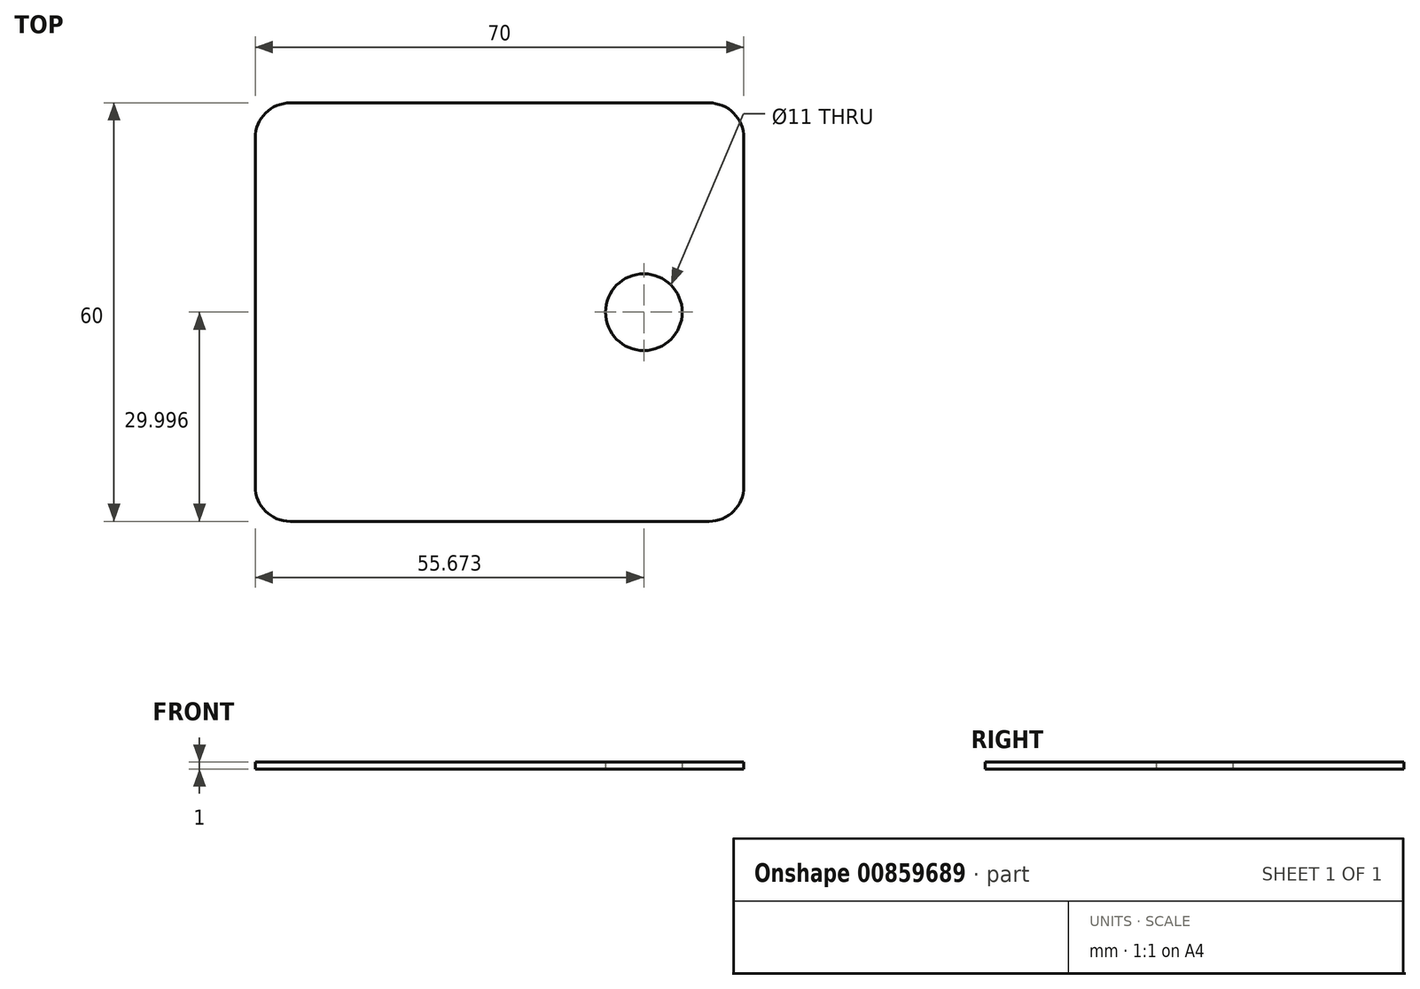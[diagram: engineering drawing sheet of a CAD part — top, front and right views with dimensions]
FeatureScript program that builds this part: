
annotation { "Feature Type Name" : "Feature", "Feature Type Description" : "" }
export const myFeature = defineFeature(function(context is Context, id is Id, definition is map)
    precondition{}
    {
        {
            var Q0;
            Q0=qCreatedBy(makeId("Top.planeOp"),FACE);
            var sketch = newSketch(context, id + "F0", { "sketchPlane" : qUnion([Q0])});
            skLineSegment(sketch, "E0.0.0", {"start": v(5.96, -58.05) * mm, "end": v(5.96, 1.95) * mm});
            skLineSegment(sketch, "E0.0.1", {"start": v(5.96, 1.95) * mm, "end": v(-64.04, 1.95) * mm});
            skLineSegment(sketch, "E0.0.2", {"start": v(-64.04, 1.95) * mm, "end": v(-64.04, -58.05) * mm});
            skLineSegment(sketch, "E0.0.3", {"start": v(-64.04, -58.05) * mm, "end": v(5.96, -58.05) * mm});
            skCircle(sketch, "E1.0", {"center": v(-8.37, -28.05) * mm, "radius": 5.5 * mm});
            skSolve(sketch);
        }
        {
            var Q0;
            Q0=makeQuery(id+"F0.imprint","IMPRINT",FACE,{"disambiguationData":[TD([[makeQuery(id+"F0.imprint","IMPRINT",EDGE,{"derivedFrom":sQuery(id+"F0.wireOp",EDGE,"E0.0.0")}),1.0]])]});
            extrude(context, id + "F1", {"entities" : qUnion([Q0]), "depth" : 1 * mm, "offsetDistance" : 25 * mm});
        }
        {
            var Q0;
            Q0=makeQuery(id+"F1.opExtrude","SWEPT_EDGE",EDGE,{"disambiguationData":[OSD([sQuery(id+"F0.wireOp",EDGE,"E0.0.2"),sQuery(id+"F0.wireOp",EDGE,"E0.0.3")])]});
            var Q1;
            Q1=makeQuery(id+"F1.opExtrude","SWEPT_EDGE",EDGE,{"disambiguationData":[OSD([sQuery(id+"F0.wireOp",EDGE,"E0.0.0"),sQuery(id+"F0.wireOp",EDGE,"E0.0.3")])]});
            var Q2;
            Q2=makeQuery(id+"F1.opExtrude","SWEPT_EDGE",EDGE,{"disambiguationData":[OSD([sQuery(id+"F0.wireOp",EDGE,"E0.0.0"),sQuery(id+"F0.wireOp",EDGE,"E0.0.1")])]});
            var Q3;
            Q3=makeQuery(id+"F1.opExtrude","SWEPT_EDGE",EDGE,{"disambiguationData":[OSD([sQuery(id+"F0.wireOp",EDGE,"E0.0.1"),sQuery(id+"F0.wireOp",EDGE,"E0.0.2")])]});
            fillet(context, id + "F2", {"entities" : qUnion([Q0, Q1, Q2, Q3]), "radius" : 5 * mm, "tangentPropagation" : true, "allowEdgeOverflow" : false});
        }
    });
